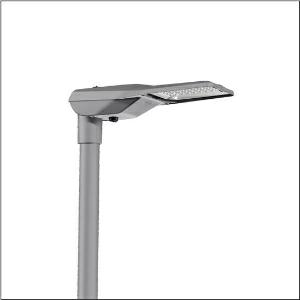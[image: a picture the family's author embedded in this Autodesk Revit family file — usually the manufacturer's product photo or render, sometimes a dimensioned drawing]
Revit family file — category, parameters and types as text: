
# Revit family: streetlight_sl_21_iq_mini___stw1_0a_5xe2e31y08gb_7efe
name_source: partatom
category: Lighting Fixtures
units: mm (PartAtom-declared; Revit-internal decimal feet)

## family parameters
Cut with Voids When Loaded = No
Host = Face
Light Source = No
Part Type = Normal
Room Calculation Point = No
Round Connector Dimension = Use Diameter
Shared = No

## types (1)
- --- (1 x LED, 5990 lm, 39.8 W, 3000K)
    Apparent Load = 40 VA
    CIE Flux Codes = 38 75 98 100 100
    Color Rendering = 70
    Color Temperature = 3000K
    Default Elevation = 1800 mm
    Description = Streetlight SL 21 iQ mini, mast luminaire, primary light control with lens, of PMMA, primary optical cover: cover, of toughened safety glass, transparent, light distribution: STW1.0a, light emission: direct distribution, primary light characteristic: asymmetric, installation type: post-top, side-entry, LED, High Power LED, rated luminous flux: 5.990lm, luminous efficacy: 151lm/W, light colour: 730, colour temperature: 3000K, control: presetting dimming logarithmic, Street-Remote, Auto-Match, Temp-Guard, Lumen-Switch, Night-Set, Smart-Wire, Light-Fading, Desk-Remote (wireless, voltage-free reading and setting of iQ features in the workshop via application-optimized NFC function/RFID function), optimised constant luminous flux control (CLO 2.0), mains connection: 220..240V, AC, 50/60Hz, start of lifetime: 40W, end of service life: 41W, reduction: 18W, luminaire housing, of diecast aluminium, powder-coated, Siteco® metallic grey (DB 702S), corrosivity category C5 mid according to DIN EN ISO 12944, please order mast flange separately, inclination adjustable: 0°, 5°, 10°, 15°, sealing non-destructively replaceable, multi-level sealing system, length: 628mm, width: 235mm, height: 110mm, mast flange for spigot size: 42mm (side-entry): 5XC10008XM4, 60/48mm (side-entry/post-top): 5XC10108XM2, 76/60mm (side-entry/post-top): 5XC10108XM1, Smart Interface below and above, protection rating (complete): IP66, insulation class (complete): insulation class II (safety insulation), certification: CE, ENEC, ENEC+, VDE, impact resistance: IK09, permissible operating ambient temperature for outdoor applications: -40..+50°C, standard-compliant lighting for roads and squares, packaging unit: 1 piece

Light Distribution: STW1.0a
    Height = 110 mm
    Lamp = 1 x LED
    Lamp Light Flux = 5990 lm
    Lamp Power = 39.8 W
    Lamp count = 1
    Length = 625 mm
    Luminous efficacy = 151 lm/W
    Manufacturer = Siteco
    ModVariant = No
    Model = 5XE2E31Y08GB
    Number of Poles = 1
    OnlyDefault = Yes
    Power Factor = 1
    Product Name = Streetlight SL 21 iQ mini | STW1.0a
    Product group = mast luminaire | pylon top
    ProductGroupID = 6100
    Protection Class = Protection class II
    Protection Degree = IP 66
    RLX_Detail_Level = 1
    RLX_Emergency_Light_Flux = 0 lm
    RLX_Emergency_Type = 0
    RLX_Emergency_Type_DB = No
    RlxData = <blob elided: 92709 chars, md5=620042ff>
    Socket = socket
    Standby Power = 0 W
    System Light Flux = 5990 lm
    System Power = 40 W
    Type Comments = factory setting: luminous flux: 100 % | dim-lin: 254 | 800 mA
    Type Image = l_1003514.jpg
    URL = http://relux.com
    VarID = @adj_062535
    Voltage = 0 V
    Weight = 0.00 kg
    Width = 234 mm

## geometry (parser evidence)
native form markers: Blend x4, Sweep x11
no freeform markers — native parametric forms only
